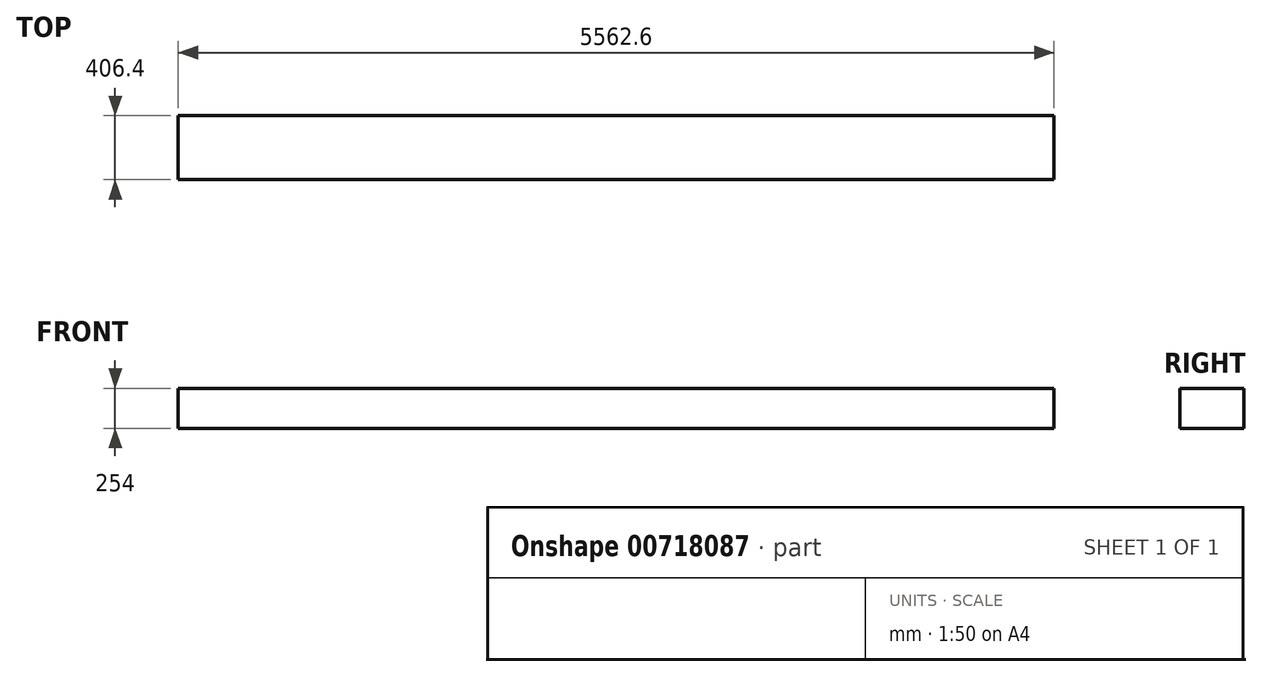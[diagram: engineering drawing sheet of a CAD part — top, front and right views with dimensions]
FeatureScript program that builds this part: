
annotation { "Feature Type Name" : "Feature", "Feature Type Description" : "" }
export const myFeature = defineFeature(function(context is Context, id is Id, definition is map)
    precondition{}
    {
        {
            var Q0;
            Q0=qCreatedBy(makeId("Right.planeOp"),FACE);
            var sketch = newSketch(context, id + "F0", { "sketchPlane" : qUnion([Q0])});
            skLineSegment(sketch, "E0.bottom", {"start": v(203.2, -127) * mm, "end": v(-203.2, -127) * mm});
            skLineSegment(sketch, "E0.top", {"start": v(203.2, 127) * mm, "end": v(-203.2, 127) * mm});
            skLineSegment(sketch, "E0.left", {"start": v(203.2, -127) * mm, "end": v(203.2, 127) * mm});
            skLineSegment(sketch, "E0.right", {"start": v(-203.2, -127) * mm, "end": v(-203.2, 127) * mm});
            skPoint(sketch, "E0.middle", {"position": v(0, 0) * mm});
            skSolve(sketch);
        }
        {
            var Q0;
            Q0=qSketchRegion(id+"F0",true);
            extrude(context, id + "F1", {"entities" : qUnion([Q0]), "depth" : 5562.6 * mm, "offsetDistance" : 25.4 * mm, "hasDraft" : true, "draftAngle" : 0 * degree});
        }
    });
